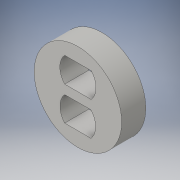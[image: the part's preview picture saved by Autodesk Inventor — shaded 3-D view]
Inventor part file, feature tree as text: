
AUTODESK INVENTOR PART (.ipt)
format: ipt  version: 2016 (Build 200138000, 138)  size: 113,664 bytes
history: native  units: in
note: dims shown in document units (in); Inventor stores cm internally (conversion verified against a paired STEP export)
features: extrude x1, sketch x1
ambient origin geometry x8: Origin, YZ Plane, XZ Plane, XY Plane, X Axis, Y Axis, Z Axis, Center Point
bodies: Solid1 (feature_tree)
feature tree (2):
  extrude  "Extrusion1"  Depth=0.198in
  sketch  "Sketch1"  dims[d0=0.198in d2=0.198in d3=0.186in d8=0.1381in d9=0.1381in d10=0.0063in d11=0.196in d12=0.184in d15=0.196in d16=0.1384in d17=0.1384in d18=0.266in d19=0.18in d20=0.0in]
